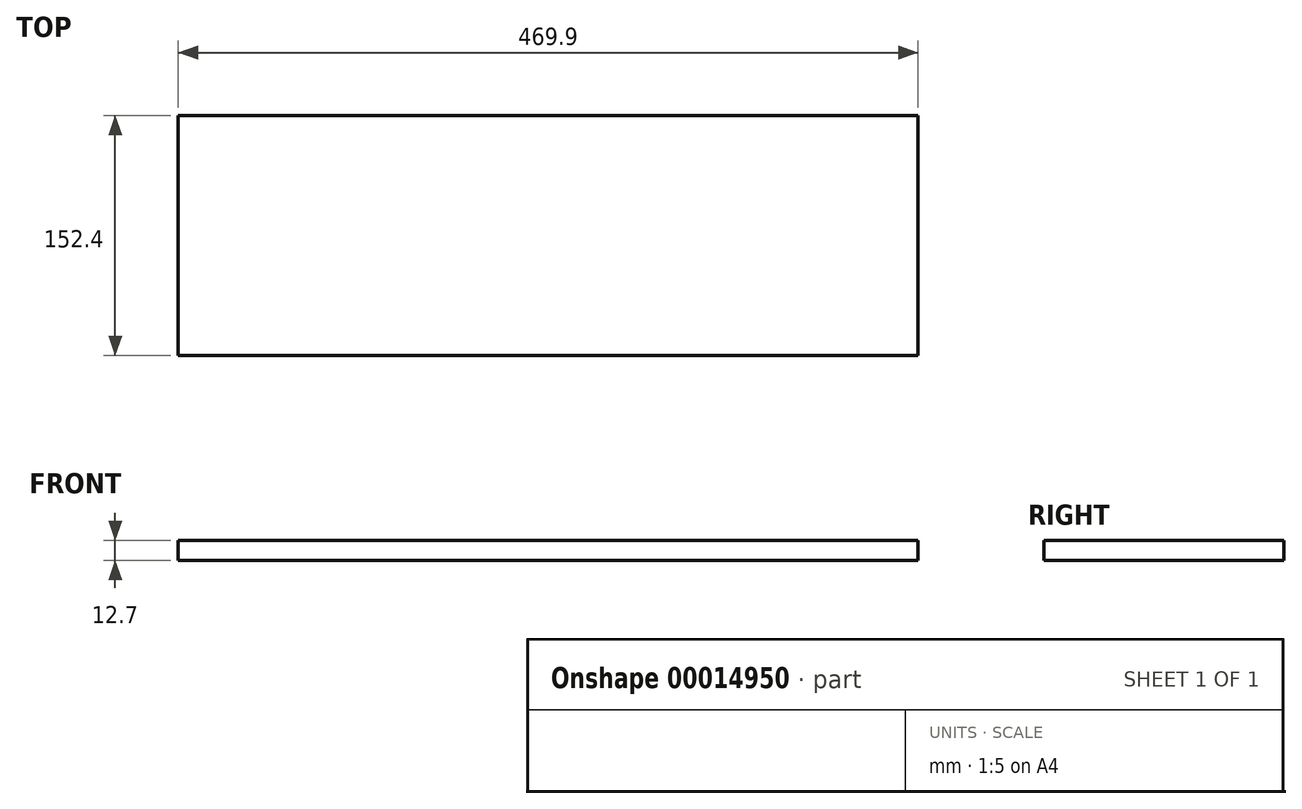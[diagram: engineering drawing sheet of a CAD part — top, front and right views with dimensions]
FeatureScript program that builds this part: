
annotation { "Feature Type Name" : "Feature", "Feature Type Description" : "" }
export const myFeature = defineFeature(function(context is Context, id is Id, definition is map)
    precondition{}
    {
        {
            var Q0;
            Q0=qCreatedBy(makeId("Top.planeOp"),FACE);
            var sketch = newSketch(context, id + "F0", { "sketchPlane" : qUnion([Q0])});
            skLineSegment(sketch, "E0.bottom", {"start": v(-223.28, 29.75) * mm, "end": v(246.62, 29.75) * mm});
            skLineSegment(sketch, "E0.top", {"start": v(-223.28, -122.65) * mm, "end": v(246.62, -122.65) * mm});
            skLineSegment(sketch, "E0.left", {"start": v(-223.28, 29.75) * mm, "end": v(-223.28, -122.65) * mm});
            skLineSegment(sketch, "E0.right", {"start": v(246.62, 29.75) * mm, "end": v(246.62, -122.65) * mm});
            skSolve(sketch);
        }
        {
            var Q0;
            Q0=makeQuery(id+"F0.imprint","IMPRINT",FACE,{"disambiguationData":[TD([[makeQuery(id+"F0.imprint","IMPRINT",EDGE,{"derivedFrom":sQuery(id+"F0.wireOp",EDGE,"E0.bottom")}),-1.0]])]});
            extrude(context, id + "F1", {"entities" : qUnion([Q0]), "depth" : 12.7 * mm});
        }
    });
